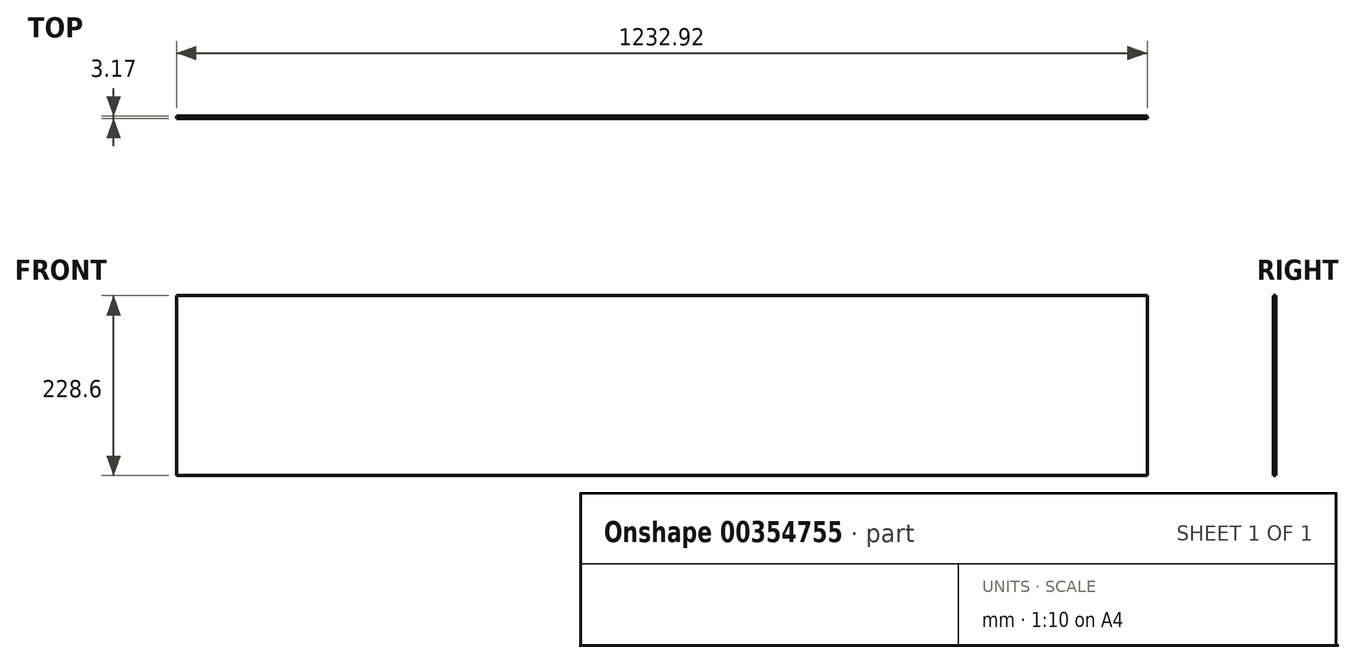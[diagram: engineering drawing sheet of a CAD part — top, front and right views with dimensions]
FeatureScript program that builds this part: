
annotation { "Feature Type Name" : "Feature", "Feature Type Description" : "" }
export const myFeature = defineFeature(function(context is Context, id is Id, definition is map)
    precondition{}
    {
        {
            var Q0;
            Q0=qCreatedBy(makeId("Front.planeOp"),FACE);
            var sketch = newSketch(context, id + "F0", { "sketchPlane" : qUnion([Q0])});
            skLineSegment(sketch, "E0.bottom", {"start": v(616.46, 114.3) * mm, "end": v(-616.46, 114.3) * mm});
            skLineSegment(sketch, "E0.top", {"start": v(616.46, -114.3) * mm, "end": v(-616.46, -114.3) * mm});
            skLineSegment(sketch, "E0.left", {"start": v(616.46, 114.3) * mm, "end": v(616.46, -114.3) * mm});
            skLineSegment(sketch, "E0.right", {"start": v(-616.46, 114.3) * mm, "end": v(-616.46, -114.3) * mm});
            skPoint(sketch, "E0.middle", {"position": v(0, 0) * mm});
            skSolve(sketch);
        }
        {
            var Q0;
            Q0 = qSketchRegion(id + "F0", true);
            extrude(context, id + "F1", {"entities" : qUnion([Q0]), "depth" : 3.17 * mm});
        }
    });
